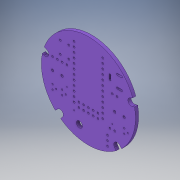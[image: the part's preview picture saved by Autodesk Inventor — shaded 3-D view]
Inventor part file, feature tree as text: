
AUTODESK INVENTOR PART (.ipt)
format: ipt  version: 2018 (Build 220112000, 112)  size: 353,280 bytes
history: native  units: in
note: dims shown in document units (in); Inventor stores cm internally (conversion verified against a paired STEP export)
features: extrude x1, sketch x1
ambient origin geometry x8: Origin, YZ Plane, XZ Plane, XY Plane, X Axis, Y Axis, Z Axis, Center Point
bodies: Body1 (feature_tree)
feature tree (2):
  extrude  "Extrusion2"  Depth=0.0657in TaperAngle=0.0deg
  sketch  "Sketch1"  dims[d2=0.7874in d4=0.1in d5=1.9685in d7=0.1in d10=0.0657in d11=0.0in d12=0.1054in d13=0.1064in d14=0.9324in d15=0.9323in d16=0.9259in d17=0.918in d18=0.3406in d19=0.3392in d20=0.0718in d21=0.0713in d22=0.0707in d23=0.0717in d24=0.4018in]
